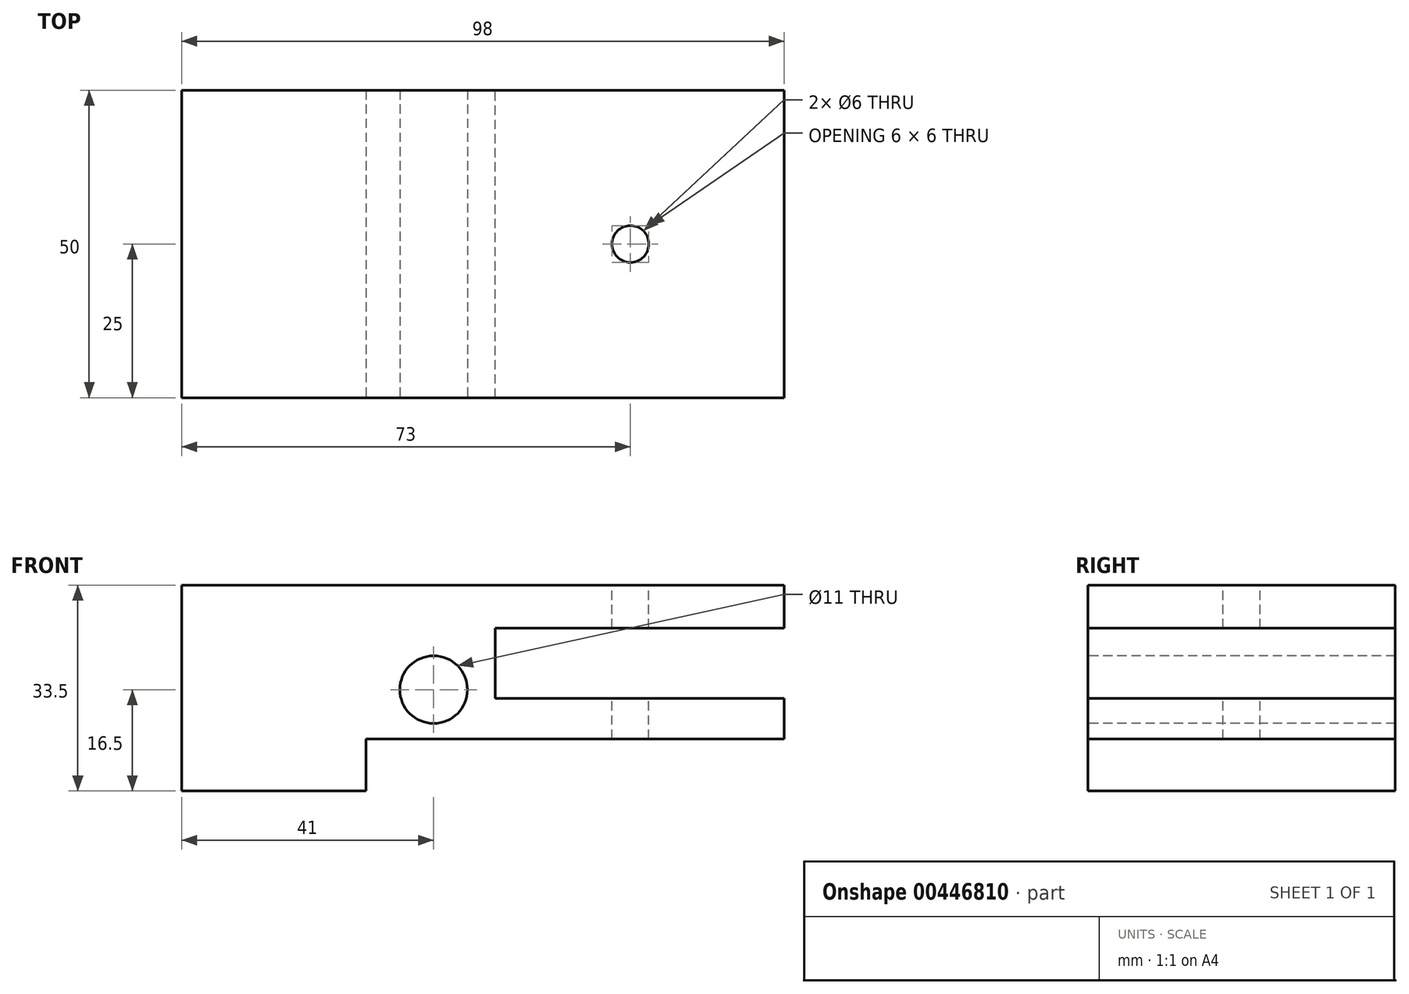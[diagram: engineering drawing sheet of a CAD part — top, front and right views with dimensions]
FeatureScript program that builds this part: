
annotation { "Feature Type Name" : "Feature", "Feature Type Description" : "" }
export const myFeature = defineFeature(function(context is Context, id is Id, definition is map)
    precondition{}
    {
        {
            var Q0;
            Q0=qCreatedBy(makeId("Front.planeOp"),FACE);
            var sketch = newSketch(context, id + "F0", { "sketchPlane" : qUnion([Q0])});
            skLineSegment(sketch, "E0.bottom", {"start": v(-183, 33.5) * mm, "end": v(183, 33.5) * mm});
            skLineSegment(sketch, "E0.top", {"start": v(-183, 0) * mm, "end": v(183, 0) * mm});
            skLineSegment(sketch, "E0.left", {"start": v(-183, 33.5) * mm, "end": v(-183, 0) * mm});
            skLineSegment(sketch, "E0.right", {"start": v(183, 33.5) * mm, "end": v(183, 0) * mm});
            skSolve(sketch);
        }
        {
            var Q0;
            Q0=makeQuery(id+"F0.imprint","IMPRINT",FACE,{"disambiguationData":[TD([[makeQuery(id+"F0.imprint","IMPRINT",EDGE,{"derivedFrom":sQuery(id+"F0.wireOp",EDGE,"E0.bottom")}),-1.0]])]});
            extrude(context, id + "F1", {"entities" : qUnion([Q0]), "endBound" : BoundingType.SYMMETRIC, "depth" : 50 * mm});
        }
        {
            var Q0;
            Q0=makeQuery(id+"F1.opExtrude","SWEPT_FACE",FACE,{"disambiguationData":[OSD([sQuery(id+"F0.wireOp",EDGE,"E0.right")])]});
            var sketch = newSketch(context, id + "F2", { "sketchPlane" : qUnion([Q0])});
            skLineSegment(sketch, "E1.bottom", {"start": v(-25, 26.5) * mm, "end": v(25, 26.5) * mm});
            skLineSegment(sketch, "E1.top", {"start": v(-25, 15.1) * mm, "end": v(25, 15.1) * mm});
            skLineSegment(sketch, "E1.left", {"start": v(-25, 26.5) * mm, "end": v(-25, 15.1) * mm});
            skLineSegment(sketch, "E1.right", {"start": v(25, 26.5) * mm, "end": v(25, 15.1) * mm});
            skSolve(sketch);
        }
        {
            var Q0;
            Q0=makeQuery(id+"F2.imprint","IMPRINT",FACE,{"disambiguationData":[TD([[makeQuery(id+"F2.imprint","IMPRINT",EDGE,{"derivedFrom":sQuery(id+"F2.wireOp",EDGE,"E1.bottom")}),-1.0]])]});
            extrude(context, id + "F3", {"entities" : qUnion([Q0]), "operationType" : NewBodyOperationType.REMOVE, "oppositeDirection" : true, "depth" : 47 * mm});
        }
        {
            var Q0;
            Q0=makeQuery(id+"F1.opExtrude","SWEPT_FACE",FACE,{"disambiguationData":[OSD([sQuery(id+"F0.wireOp",EDGE,"E0.left")])]});
            var sketch = newSketch(context, id + "F4", { "sketchPlane" : qUnion([Q0])});
            skLineSegment(sketch, "E2.bottom", {"start": v(-25, 26.5) * mm, "end": v(25, 26.5) * mm});
            skLineSegment(sketch, "E2.top", {"start": v(-25, 15.1) * mm, "end": v(25, 15.1) * mm});
            skLineSegment(sketch, "E2.left", {"start": v(-25, 26.5) * mm, "end": v(-25, 15.1) * mm});
            skLineSegment(sketch, "E2.right", {"start": v(25, 26.5) * mm, "end": v(25, 15.1) * mm});
            skSolve(sketch);
        }
        {
            var Q0;
            Q0=makeQuery(id+"F4.imprint","IMPRINT",FACE,{"disambiguationData":[TD([[makeQuery(id+"F4.imprint","IMPRINT",EDGE,{"derivedFrom":sQuery(id+"F4.wireOp",EDGE,"E2.bottom")}),-1.0]])]});
            extrude(context, id + "F5", {"entities" : qUnion([Q0]), "operationType" : NewBodyOperationType.REMOVE, "oppositeDirection" : true, "depth" : 53 * mm});
        }
        {
            var Q0;
            Q0=makeQuery(id+"F1.opExtrude","CAP_FACE",FACE,{"disambiguationData":[OSD([sQuery(id+"F0.wireOp",EDGE,"E0.bottom"),sQuery(id+"F0.wireOp",EDGE,"E0.top"),sQuery(id+"F0.wireOp",EDGE,"E0.left"),sQuery(id+"F0.wireOp",EDGE,"E0.right")])],"isStart":false});
            var sketch = newSketch(context, id + "F6", { "sketchPlane" : qUnion([Q0])});
            skLineSegment(sketch, "E3.bottom", {"start": v(183, 0) * mm, "end": v(115, 0) * mm});
            skLineSegment(sketch, "E3.top", {"start": v(183, 8.5) * mm, "end": v(115, 8.5) * mm});
            skLineSegment(sketch, "E3.left", {"start": v(183, 0) * mm, "end": v(183, 8.5) * mm});
            skLineSegment(sketch, "E3.right", {"start": v(115, 0) * mm, "end": v(115, 8.5) * mm});
            skLineSegment(sketch, "E4.bottom", {"start": v(-183, 0) * mm, "end": v(-115, 0) * mm});
            skLineSegment(sketch, "E4.top", {"start": v(-183, 8.5) * mm, "end": v(-115, 8.5) * mm});
            skLineSegment(sketch, "E4.left", {"start": v(-183, 0) * mm, "end": v(-183, 8.5) * mm});
            skLineSegment(sketch, "E4.right", {"start": v(-115, 0) * mm, "end": v(-115, 8.5) * mm});
            skSolve(sketch);
        }
        {
            var Q0;
            Q0=makeQuery(id+"F6.imprint","IMPRINT",FACE,{"disambiguationData":[TD([[makeQuery(id+"F6.imprint","IMPRINT",EDGE,{"derivedFrom":sQuery(id+"F6.wireOp",EDGE,"E4.bottom")}),1.0]])]});
            var Q1;
            Q1=makeQuery(id+"F6.imprint","IMPRINT",FACE,{"disambiguationData":[TD([[makeQuery(id+"F6.imprint","IMPRINT",EDGE,{"derivedFrom":sQuery(id+"F6.wireOp",EDGE,"E3.bottom")}),1.0]])]});
            extrude(context, id + "F7", {"entities" : qUnion([Q0, Q1]), "operationType" : NewBodyOperationType.REMOVE, "oppositeDirection" : true, "depth" : 100 * mm});
        }
        {
            var Q0;
            Q0=makeQuery(id+"F1.opExtrude","CAP_FACE",FACE,{"disambiguationData":[OSD([sQuery(id+"F0.wireOp",EDGE,"E0.bottom"),sQuery(id+"F0.wireOp",EDGE,"E0.top"),sQuery(id+"F0.wireOp",EDGE,"E0.left"),sQuery(id+"F0.wireOp",EDGE,"E0.right")])],"isStart":false});
            var sketch = newSketch(context, id + "F8", { "sketchPlane" : qUnion([Q0])});
            skLineSegment(sketch, "E5.bottom", {"start": v(-85, 33.5) * mm, "end": v(85, 33.5) * mm});
            skLineSegment(sketch, "E5.top", {"start": v(-85, 12.5) * mm, "end": v(85, 12.5) * mm});
            skLineSegment(sketch, "E5.left", {"start": v(-85, 33.5) * mm, "end": v(-85, 12.5) * mm});
            skLineSegment(sketch, "E5.right", {"start": v(85, 33.5) * mm, "end": v(85, 12.5) * mm});
            skSolve(sketch);
        }
        {
            var Q0;
            Q0=makeQuery(id+"F8.imprint","IMPRINT",FACE,{"disambiguationData":[TD([[makeQuery(id+"F8.imprint","IMPRINT",EDGE,{"derivedFrom":sQuery(id+"F8.wireOp",EDGE,"E5.bottom")}),-1.0]])]});
            extrude(context, id + "F9", {"entities" : qUnion([Q0]), "operationType" : NewBodyOperationType.REMOVE, "oppositeDirection" : true, "depth" : 79.8 * mm});
        }
        {
            var Q0;
            Q0=makeQuery(id+"F9.boolean.opBoolean","COPY",FACE,{"derivedFrom":makeQuery(id+"F9.opExtrude","SWEPT_FACE",FACE,{"disambiguationData":[OSD([sQuery(id+"F8.wireOp",EDGE,"E5.top")])]})});
            var sketch = newSketch(context, id + "F10", { "sketchPlane" : qUnion([Q0])});
            skCircle(sketch, "E6", {"center": v(0, 0) * mm, "radius": 11.5 * mm});
            skSolve(sketch);
        }
        {
            var Q0;
            Q0=makeQuery(id+"F10.imprint","IMPRINT",FACE,{"disambiguationData":[TD([[makeQuery(id+"F10.imprint","IMPRINT",EDGE,{"derivedFrom":sQuery(id+"F10.wireOp",EDGE,"E6")}),1.0]])]});
            extrude(context, id + "F11", {"entities" : qUnion([Q0]), "operationType" : NewBodyOperationType.REMOVE, "oppositeDirection" : true, "depth" : 56 * mm});
        }
        {
            var Q0;
            Q0=makeQuery(id+"F9.boolean.opBoolean","COPY",FACE,{"derivedFrom":makeQuery(id+"F9.opExtrude","SWEPT_FACE",FACE,{"disambiguationData":[OSD([sQuery(id+"F8.wireOp",EDGE,"E5.right")])]})});
            var sketch = newSketch(context, id + "F12", { "sketchPlane" : qUnion([Q0])});
            skLineSegment(sketch, "E7.bottom", {"start": v(39.14, -21) * mm, "end": v(-38.9, -21) * mm});
            skLineSegment(sketch, "E7.top", {"start": v(39.14, 51.1) * mm, "end": v(-38.9, 51.1) * mm});
            skLineSegment(sketch, "E7.left", {"start": v(39.14, -21) * mm, "end": v(39.14, 51.1) * mm});
            skLineSegment(sketch, "E7.right", {"start": v(-38.9, -21) * mm, "end": v(-38.9, 51.1) * mm});
            skSolve(sketch);
        }
        {
            var Q0;
            Q0=qSketchRegion(id+"F12",true);
            extrude(context, id + "F13", {"entities" : qUnion([Q0]), "operationType" : NewBodyOperationType.REMOVE, "endBound" : BoundingType.UP_TO_NEXT, "depth" : 25 * mm});
        }
        {
            var Q0;
            {var subQ0=sQuery(id+"F0.wireOp",EDGE,"E0.right");var subQ3=sQuery(id+"F0.wireOp",EDGE,"E0.bottom");Q0=makeQuery(id+"F9.boolean.opBoolean","SPLIT",FACE,{"disambiguationData":[TD([makeQuery(id+"F1.opExtrude","SWEPT_FACE",FACE,{"disambiguationData":[OSD([subQ0])]})])],"derivedFrom":makeQuery(id+"F1.opExtrude","SWEPT_FACE",FACE,{"disambiguationData":[OSD([subQ3])]})});}
            var sketch = newSketch(context, id + "F14", { "sketchPlane" : qUnion([Q0])});
            skLineSegment(sketch, "E8.0.0", {"start": v(183, -25) * mm, "end": v(183, 25) * mm});
            skLineSegment(sketch, "E8.0.1", {"start": v(183, 25) * mm, "end": v(136, 25) * mm});
            skLineSegment(sketch, "E8.0.2", {"start": v(136, 25) * mm, "end": v(136, -25) * mm});
            skLineSegment(sketch, "E8.0.3", {"start": v(136, -25) * mm, "end": v(183, -25) * mm});
            skCircle(sketch, "E9", {"center": v(158, 0) * mm, "radius": 3 * mm});
            skSolve(sketch);
        }
        {
            var Q0;
            Q0=makeQuery(id+"F14.imprint","IMPRINT",FACE,{"disambiguationData":[TD([[makeQuery(id+"F14.imprint","IMPRINT",EDGE,{"derivedFrom":sQuery(id+"F14.wireOp",EDGE,"E9")}),1.0]])]});
            extrude(context, id + "F15", {"entities" : qUnion([Q0]), "operationType" : NewBodyOperationType.REMOVE, "oppositeDirection" : true, "depth" : 50 * mm});
        }
        {
            var Q0;
            Q0=makeQuery(id+"F8.imprint","IMPRINT",FACE,{"disambiguationData":[TD([[makeQuery(id+"F8.imprint","IMPRINT",EDGE,{"derivedFrom":sQuery(id+"F8.wireOp",EDGE,"E5.top")}),-1.0]])]});
            var sketch = newSketch(context, id + "F16", { "sketchPlane" : qUnion([Q0])});
            skCircle(sketch, "E10", {"center": v(126, 16.5) * mm, "radius": 5.5 * mm});
            skSolve(sketch);
        }
        {
            var Q0;
            Q0=qSketchRegion(id+"F16",true);
            extrude(context, id + "F17", {"entities" : qUnion([Q0]), "operationType" : NewBodyOperationType.REMOVE, "oppositeDirection" : true, "depth" : 100 * mm});
        }
    });
